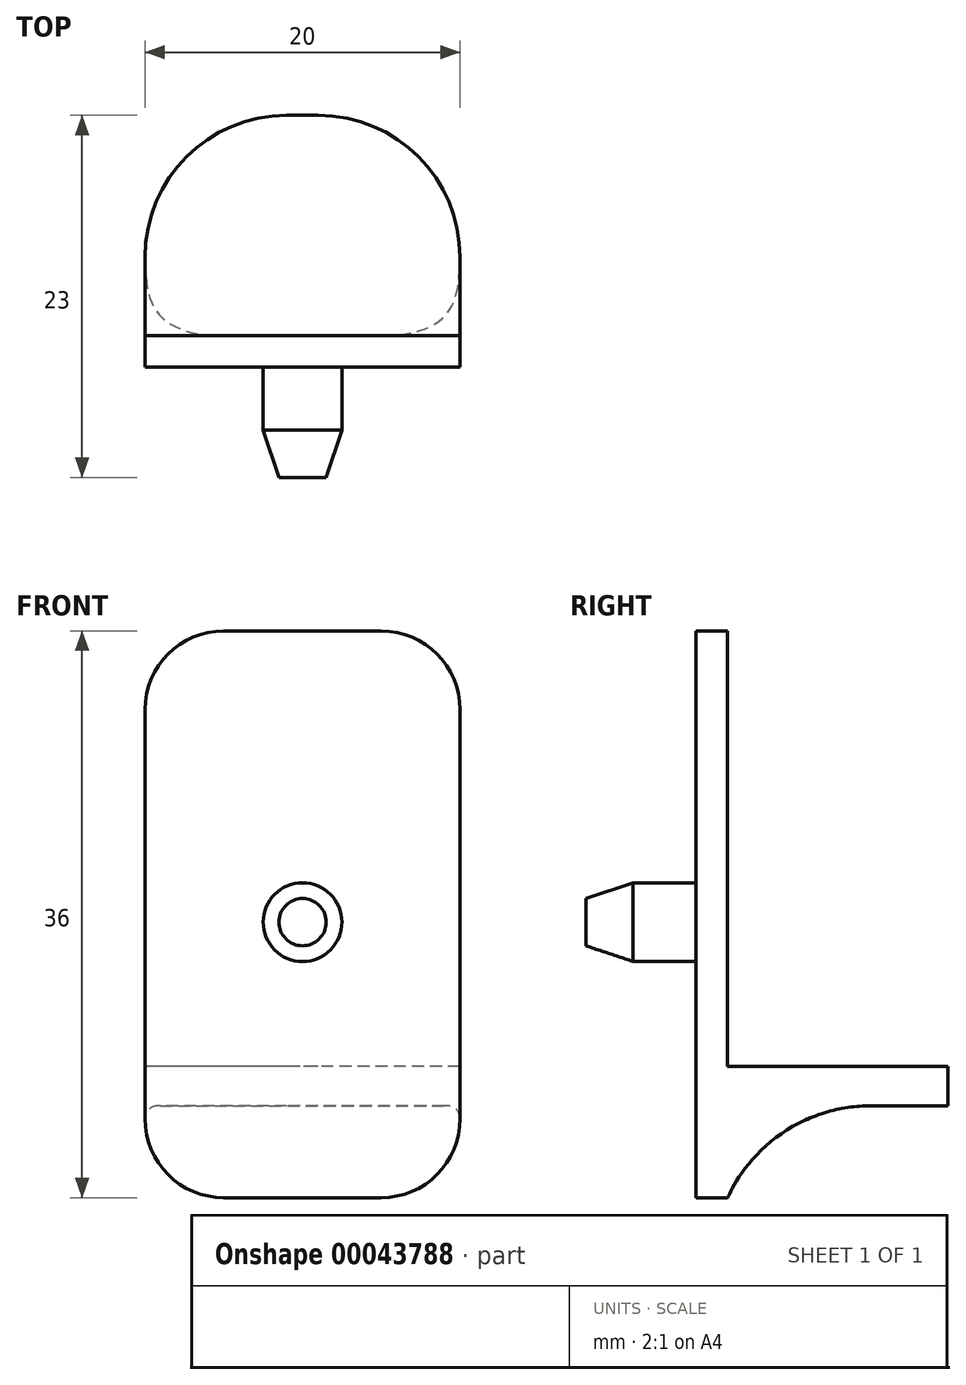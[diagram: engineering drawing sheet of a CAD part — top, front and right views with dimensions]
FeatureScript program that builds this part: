
annotation { "Feature Type Name" : "Feature", "Feature Type Description" : "" }
export const myFeature = defineFeature(function(context is Context, id is Id, definition is map)
    precondition{}
    {
        {
            var Q0;
            Q0=qCreatedBy(makeId("Front.planeOp"),FACE);
            var sketch = newSketch(context, id + "F0", { "sketchPlane" : qUnion([Q0])});
            skCircle(sketch, "E0", {"center": v(0, 0) * mm, "radius": 2.5 * mm});
            skLineSegment(sketch, "E1.bottom", {"start": v(-10, 18.5) * mm, "end": v(10, 18.5) * mm});
            skLineSegment(sketch, "E1.top", {"start": v(-10, -17.5) * mm, "end": v(10, -17.5) * mm});
            skLineSegment(sketch, "E1.left", {"start": v(-10, 18.5) * mm, "end": v(-10, -17.5) * mm});
            skLineSegment(sketch, "E1.right", {"start": v(10, 18.5) * mm, "end": v(10, -17.5) * mm});
            skLineSegment(sketch, "E2", {"start": v(10, -2.5) * mm, "end": v(-10, -2.5) * mm, "construction": true});
            skLineSegment(sketch, "E3", {"start": v(10, -9.16) * mm, "end": v(-10, -9.16) * mm, "construction": true});
            skSolve(sketch);
        }
        {
            var Q0;
            Q0=makeQuery(id+"F0.imprint","IMPRINT",FACE,{"disambiguationData":[TD([[makeQuery(id+"F0.imprint","IMPRINT",EDGE,{"derivedFrom":sQuery(id+"F0.wireOp",EDGE,"E0")}),1.0]])]});
            extrude(context, id + "F1", {"entities" : qUnion([Q0]), "depth" : 7 * mm});
        }
        {
            var Q0;
            Q0=makeQuery(id+"F1.opExtrude","CAP_EDGE",EDGE,{"disambiguationData":[OSD([sQuery(id+"F0.wireOp",EDGE,"E0")])],"isStart":false});
            chamfer(context, id + "F2", {"entities" : qUnion([Q0]), "chamferType" : ChamferType.TWO_OFFSETS, "width1" : 1 * mm, "oppositeDirection" : false, "width2" : 3 * mm, "tangentPropagation" : true});
        }
        {
            var Q0;
            Q0=makeQuery(id+"F0.imprint","IMPRINT",FACE,{"disambiguationData":[TD([[makeQuery(id+"F0.imprint","IMPRINT",EDGE,{"derivedFrom":sQuery(id+"F0.wireOp",EDGE,"E0")}),1.0]])]});
            var Q1;
            Q1=makeQuery(id+"F0.imprint","IMPRINT",FACE,{"disambiguationData":[TD([[makeQuery(id+"F0.imprint","IMPRINT",EDGE,{"derivedFrom":sQuery(id+"F0.wireOp",EDGE,"E0")}),-1.0]])]});
            extrude(context, id + "F3", {"entities" : qUnion([Q0, Q1]), "operationType" : NewBodyOperationType.ADD, "oppositeDirection" : true, "depth" : 2 * mm});
        }
        {
            var Q0;
            Q0=makeQuery(id+"F3.opExtrude","CAP_FACE",FACE,{"disambiguationData":[OSD([sQuery(id+"F0.wireOp",EDGE,"E1.bottom"),sQuery(id+"F0.wireOp",EDGE,"E1.top"),sQuery(id+"F0.wireOp",EDGE,"E1.left"),sQuery(id+"F0.wireOp",EDGE,"E1.right")])],"isStart":false});
            var sketch = newSketch(context, id + "F4", { "sketchPlane" : qUnion([Q0])});
            skLineSegment(sketch, "E4.bottom", {"start": v(-10, -9.16) * mm, "end": v(10, -9.16) * mm});
            skLineSegment(sketch, "E4.top", {"start": v(-10, -11.66) * mm, "end": v(10, -11.66) * mm});
            skLineSegment(sketch, "E4.left", {"start": v(-10, -9.16) * mm, "end": v(-10, -11.66) * mm});
            skLineSegment(sketch, "E4.right", {"start": v(10, -9.16) * mm, "end": v(10, -11.66) * mm});
            skSolve(sketch);
        }
        {
            var Q0;
            Q0 = qSketchRegion(id + "F4", true);
            extrude(context, id + "F5", {"entities" : qUnion([Q0]), "operationType" : NewBodyOperationType.ADD, "depth" : 14 * mm});
        }
        {
            var Q0;
            Q0=makeQuery(id+"F5.opExtrude","CAP_EDGE",EDGE,{"disambiguationData":[OSD([sQuery(id+"F4.wireOp",EDGE,"E4.left")])],"isStart":false});
            var Q1;
            Q1=makeQuery(id+"F5.opExtrude","CAP_EDGE",EDGE,{"disambiguationData":[OSD([sQuery(id+"F4.wireOp",EDGE,"E4.right")])],"isStart":false});
            fillet(context, id + "F6", {"entities" : qUnion([Q0, Q1]), "radius" : 9 * mm, "tangentPropagation" : true, "allowEdgeOverflow" : false});
        }
        {
            var Q0;
            Q0=makeQuery(id+"F3.opExtrude","SWEPT_EDGE",EDGE,{"disambiguationData":[OSD([sQuery(id+"F0.wireOp",EDGE,"E1.bottom"),sQuery(id+"F0.wireOp",EDGE,"E1.right")])]});
            var Q1;
            Q1=makeQuery(id+"F3.opExtrude","SWEPT_EDGE",EDGE,{"disambiguationData":[OSD([sQuery(id+"F0.wireOp",EDGE,"E1.top"),sQuery(id+"F0.wireOp",EDGE,"E1.right")])]});
            var Q2;
            Q2=makeQuery(id+"F3.opExtrude","SWEPT_EDGE",EDGE,{"disambiguationData":[OSD([sQuery(id+"F0.wireOp",EDGE,"E1.top"),sQuery(id+"F0.wireOp",EDGE,"E1.left")])]});
            var Q3;
            Q3=makeQuery(id+"F3.opExtrude","SWEPT_EDGE",EDGE,{"disambiguationData":[OSD([sQuery(id+"F0.wireOp",EDGE,"E1.bottom"),sQuery(id+"F0.wireOp",EDGE,"E1.left")])]});
            fillet(context, id + "F7", {"entities" : qUnion([Q0, Q1, Q2, Q3]), "radius" : 5 * mm, "tangentPropagation" : true, "allowEdgeOverflow" : false});
        }
        {
            var Q0;
            Q0=makeQuery(id+"F5.opExtrude","CAP_EDGE",EDGE,{"disambiguationData":[OSD([sQuery(id+"F4.wireOp",EDGE,"E4.top")])],"isStart":true});
            fillet(context, id + "F8", {"entities" : qUnion([Q0]), "radius" : 10 * mm, "tangentPropagation" : true, "allowEdgeOverflow" : false});
        }
    });
